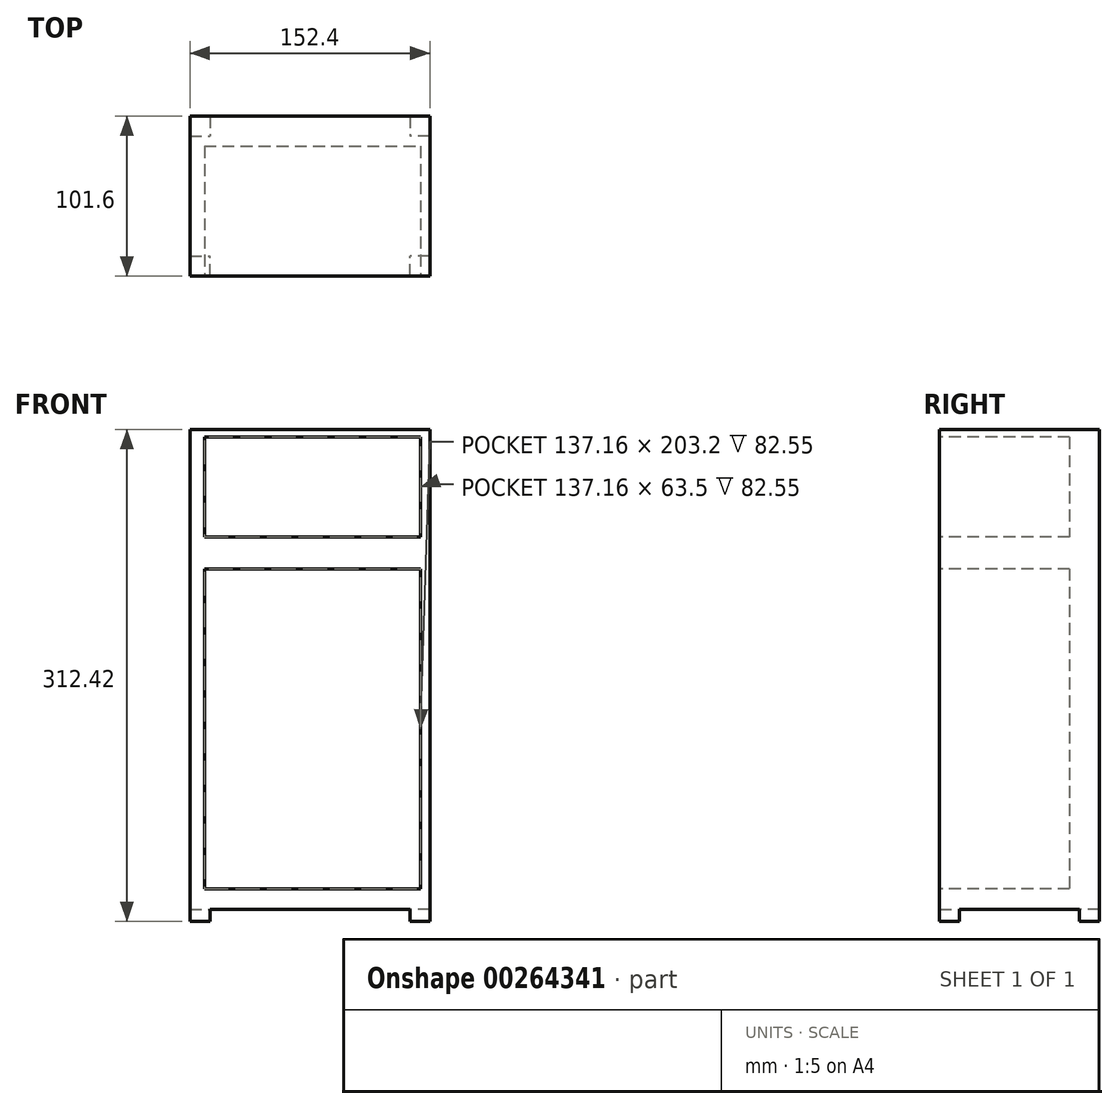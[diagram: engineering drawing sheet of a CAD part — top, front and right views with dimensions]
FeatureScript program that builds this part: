
annotation { "Feature Type Name" : "Feature", "Feature Type Description" : "" }
export const myFeature = defineFeature(function(context is Context, id is Id, definition is map)
    precondition{}
    {
        {
            var Q0;
            Q0=qCreatedBy(makeId("Front.planeOp"),FACE);
            var sketch = newSketch(context, id + "F0", { "sketchPlane" : qUnion([Q0])});
            skLineSegment(sketch, "E0.bottom", {"start": v(76.2, 152.4) * mm, "end": v(-76.2, 152.4) * mm});
            skLineSegment(sketch, "E0.top", {"start": v(76.2, -152.4) * mm, "end": v(-76.2, -152.4) * mm});
            skLineSegment(sketch, "E0.left", {"start": v(76.2, 152.4) * mm, "end": v(76.2, -152.4) * mm});
            skLineSegment(sketch, "E0.right", {"start": v(-76.2, 152.4) * mm, "end": v(-76.2, -152.4) * mm});
            skPoint(sketch, "E0.middle", {"position": v(0, 0) * mm});
            skSolve(sketch);
        }
        {
            var Q0;
            Q0 = qSketchRegion(id + "F0", true);
            extrude(context, id + "F1", {"entities" : qUnion([Q0]), "endBound" : BoundingType.SYMMETRIC, "depth" : 101.6 * mm});
        }
        {
            var Q0;
            Q0=makeQuery(id+"F1.opExtrude","CAP_FACE",FACE,{"disambiguationData":[OSD([sQuery(id+"F0.wireOp",EDGE,"E0.bottom"),sQuery(id+"F0.wireOp",EDGE,"E0.top"),sQuery(id+"F0.wireOp",EDGE,"E0.left"),sQuery(id+"F0.wireOp",EDGE,"E0.right")])],"isStart":false});
            var sketch = newSketch(context, id + "F2", { "sketchPlane" : qUnion([Q0])});
            skLineSegment(sketch, "E1.bottom", {"start": v(-66.98, 147.5) * mm, "end": v(70.18, 147.5) * mm});
            skLineSegment(sketch, "E1.top", {"start": v(-66.98, 84) * mm, "end": v(70.18, 84) * mm});
            skLineSegment(sketch, "E1.left", {"start": v(-66.98, 147.5) * mm, "end": v(-66.98, 84) * mm});
            skLineSegment(sketch, "E1.right", {"start": v(70.18, 147.5) * mm, "end": v(70.18, 84) * mm});
            skLineSegment(sketch, "E2.bottom", {"start": v(-66.98, 63.98) * mm, "end": v(70.18, 63.98) * mm});
            skLineSegment(sketch, "E2.top", {"start": v(-66.98, -139.22) * mm, "end": v(70.18, -139.22) * mm});
            skLineSegment(sketch, "E2.left", {"start": v(-66.98, 63.98) * mm, "end": v(-66.98, -139.22) * mm});
            skLineSegment(sketch, "E2.right", {"start": v(70.18, 63.98) * mm, "end": v(70.18, -139.22) * mm});
            skSolve(sketch);
        }
        {
            var Q0;
            Q0 = qSketchRegion(id + "F2", true);
            extrude(context, id + "F3", {"entities" : qUnion([Q0]), "operationType" : NewBodyOperationType.REMOVE, "oppositeDirection" : true, "depth" : 82.55 * mm});
        }
        {
            var Q0;
            Q0=makeQuery(id+"F1.opExtrude","SWEPT_FACE",FACE,{"disambiguationData":[OSD([sQuery(id+"F0.wireOp",EDGE,"E0.top")])]});
            var sketch = newSketch(context, id + "F4", { "sketchPlane" : qUnion([Q0])});
            skLineSegment(sketch, "E3.bottom", {"start": v(-76.2, 50.8) * mm, "end": v(-63.5, 50.8) * mm});
            skLineSegment(sketch, "E3.top", {"start": v(-76.2, 38.1) * mm, "end": v(-63.5, 38.1) * mm});
            skLineSegment(sketch, "E3.left", {"start": v(-76.2, 50.8) * mm, "end": v(-76.2, 38.1) * mm});
            skLineSegment(sketch, "E3.right", {"start": v(-63.5, 50.8) * mm, "end": v(-63.5, 38.1) * mm});
            skLineSegment(sketch, "E4.bottom", {"start": v(76.2, 50.8) * mm, "end": v(63.5, 50.8) * mm});
            skLineSegment(sketch, "E4.top", {"start": v(76.2, 38.1) * mm, "end": v(63.5, 38.1) * mm});
            skLineSegment(sketch, "E4.left", {"start": v(76.2, 50.8) * mm, "end": v(76.2, 38.1) * mm});
            skLineSegment(sketch, "E4.right", {"start": v(63.5, 50.8) * mm, "end": v(63.5, 38.1) * mm});
            skLineSegment(sketch, "E5.bottom", {"start": v(-76.2, -50.8) * mm, "end": v(-63.5, -50.8) * mm});
            skLineSegment(sketch, "E5.top", {"start": v(-76.2, -38.1) * mm, "end": v(-63.5, -38.1) * mm});
            skLineSegment(sketch, "E5.left", {"start": v(-76.2, -50.8) * mm, "end": v(-76.2, -38.1) * mm});
            skLineSegment(sketch, "E5.right", {"start": v(-63.5, -50.8) * mm, "end": v(-63.5, -38.1) * mm});
            skLineSegment(sketch, "E6.bottom", {"start": v(76.2, -50.8) * mm, "end": v(63.5, -50.8) * mm});
            skLineSegment(sketch, "E6.top", {"start": v(76.2, -38.1) * mm, "end": v(63.5, -38.1) * mm});
            skLineSegment(sketch, "E6.left", {"start": v(76.2, -50.8) * mm, "end": v(76.2, -38.1) * mm});
            skLineSegment(sketch, "E6.right", {"start": v(63.5, -50.8) * mm, "end": v(63.5, -38.1) * mm});
            skSolve(sketch);
        }
        {
            var Q0;
            Q0 = qSketchRegion(id + "F4", true);
            extrude(context, id + "F5", {"entities" : qUnion([Q0]), "operationType" : NewBodyOperationType.ADD, "depth" : 7.62 * mm});
        }
    });
